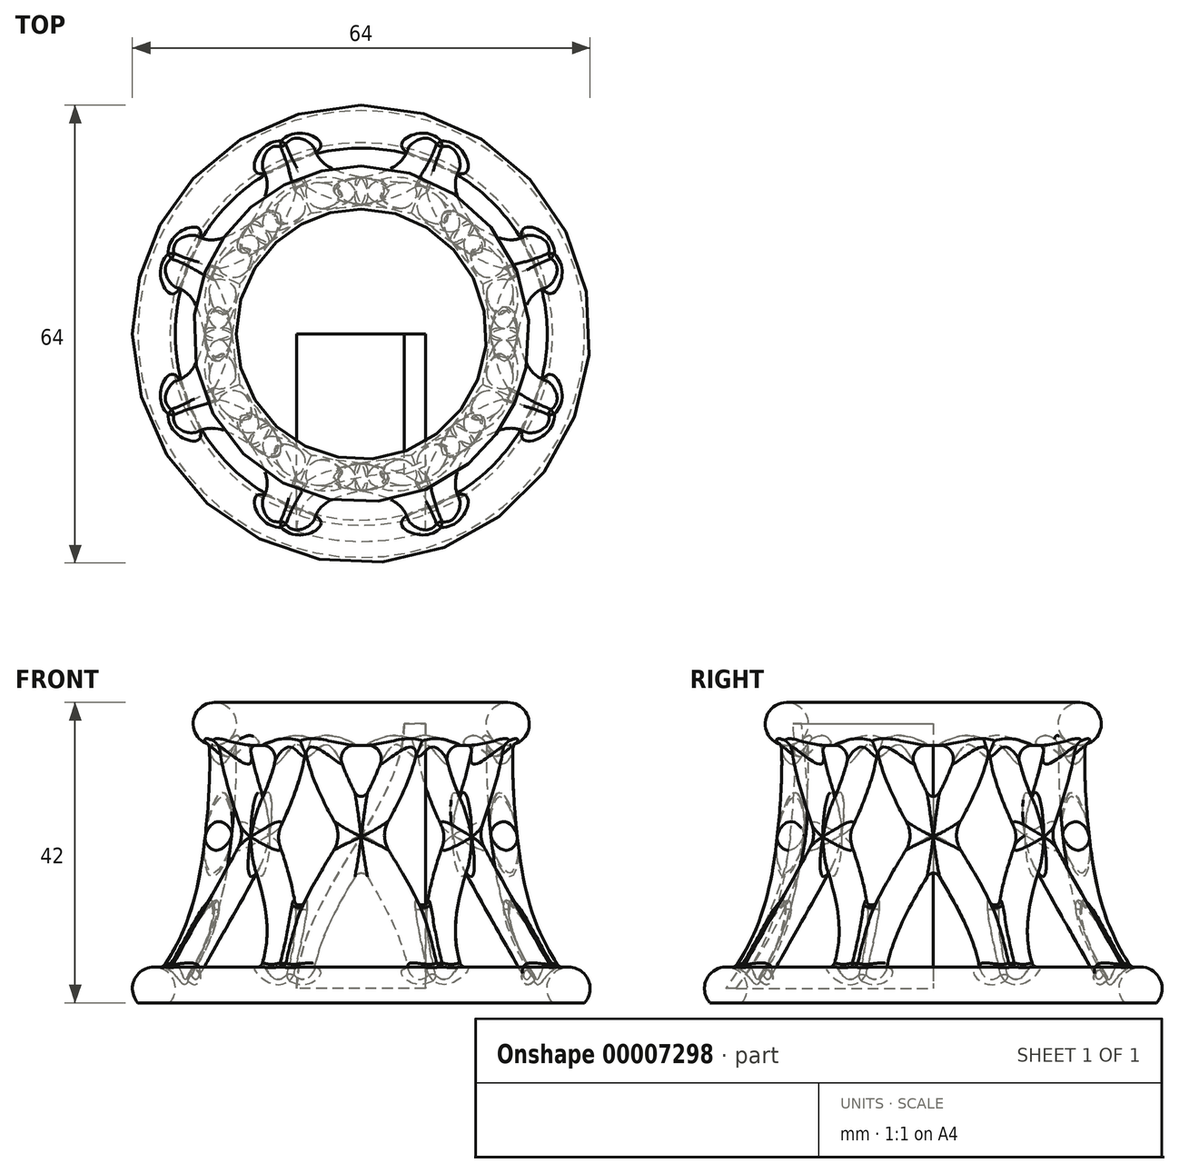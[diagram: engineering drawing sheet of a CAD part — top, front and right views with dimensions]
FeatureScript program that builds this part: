
annotation { "Feature Type Name" : "Feature", "Feature Type Description" : "" }
export const myFeature = defineFeature(function(context is Context, id is Id, definition is map)
    precondition{}
    {
        {
            var Q0;
            Q0=qCreatedBy(makeId("Front.planeOp"),FACE);
            var sketch = newSketch(context, id + "F0", { "sketchPlane" : qUnion([Q0])});
            skLineSegment(sketch, "E0", {"start": v(0, 0) * mm, "end": v(0, 10.66) * mm, "construction": true});
            skArc(sketch, "E1", {"start": v(31.24, 0) * mm, "mid": v(29, 5) * mm, "end": v(26.76, 0) * mm});
            skLineSegment(sketch, "E2", {"start": v(26.76, 0) * mm, "end": v(31.24, 0) * mm});
            skLineSegment(sketch, "E3", {"start": v(29, 2) * mm, "end": v(32, 2) * mm, "construction": true});
            skSolve(sketch);
        }
        {
            var Q0;
            Q0=makeQuery(id+"F0.imprint","IMPRINT",FACE,{"disambiguationData":[TD([[makeQuery(id+"F0.imprint","IMPRINT",EDGE,{"derivedFrom":sQuery(id+"F0.wireOp",EDGE,"E1")}),1.0]])]});
            var Q1;
            Q1=sQuery(id+"F0.wireOp",EDGE,"E0");
            revolve(context, id + "F1", {"entities" : qUnion([Q0]), "axis" : qUnion([Q1]), "revolveType" : RevolveType.FULL});
        }
        {
            var Q0;
            Q0=qCreatedBy(makeId("Front.planeOp"),FACE);
            var sketch = newSketch(context, id + "F2", { "sketchPlane" : qUnion([Q0])});
            skCircle(sketch, "E4", {"center": v(20.5, 39) * mm, "radius": 3 * mm});
            skLineSegment(sketch, "E5", {"start": v(20.5, 39) * mm, "end": v(17.5, 39) * mm, "construction": true});
            skLineSegment(sketch, "E6", {"start": v(20.5, 39) * mm, "end": v(20.5, 42) * mm, "construction": true});
            skSolve(sketch);
        }
        {
            var Q0;
            Q0=makeQuery(id+"F2.imprint","IMPRINT",FACE,{"disambiguationData":[TD([[makeQuery(id+"F2.imprint","IMPRINT",EDGE,{"derivedFrom":sQuery(id+"F2.wireOp",EDGE,"E4")}),1.0]])]});
            var Q1;
            Q1=sQuery(id+"F0.wireOp",EDGE,"E0");
            revolve(context, id + "F3", {"entities" : qUnion([Q0]), "axis" : qUnion([Q1]), "revolveType" : RevolveType.FULL});
        }
        {
            var Q0;
            Q0=qCreatedBy(makeId("Front.planeOp"),FACE);
            var sketch = newSketch(context, id + "F4", { "sketchPlane" : qUnion([Q0])});
            skFitSpline(sketch, "E7", {"points": [v(6, 39) * mm, v(-9, 2) * mm], "startDerivative": vector(0, -36) * mm, "endDerivative": vector(0, -39) * mm});
            skLineSegment(sketch, "E8", {"start": v(0, 0) * mm, "end": v(-9, 0) * mm, "construction": true});
            skLineSegment(sketch, "E9", {"start": v(-9, 0) * mm, "end": v(-9, 2) * mm, "construction": true});
            skLineSegment(sketch, "E10", {"start": v(-9, 2) * mm, "end": v(-9, 39) * mm, "construction": true});
            skLineSegment(sketch, "E11", {"start": v(-9, 39) * mm, "end": v(6, 39) * mm, "construction": true});
            skLineSegment(sketch, "E12", {"start": v(0, 0) * mm, "end": v(0, 39) * mm, "construction": true});
            skLineSegment(sketch, "E13", {"start": v(6, 39) * mm, "end": v(6, 46.33) * mm, "construction": true});
            skLineSegment(sketch, "E14", {"start": v(6, 39) * mm, "end": v(9, 39) * mm});
            skLineSegment(sketch, "E15", {"start": v(9, 39) * mm, "end": v(9, 2) * mm});
            skLineSegment(sketch, "E16", {"start": v(9, 2) * mm, "end": v(-9, 2) * mm});
            skSolve(sketch);
        }
        {
            var Q0;
            Q0=qCreatedBy(makeId("Front.planeOp"),FACE);
            var sketch = newSketch(context, id + "F5", { "sketchPlane" : qUnion([Q0])});
            skFitSpline(sketch, "E17", {"points": [v(20.5, 39) * mm, v(29, 2) * mm], "startDerivative": vector(-3.15, -36) * mm, "endDerivative": vector(33.6, -48) * mm});
            skLineSegment(sketch, "E18", {"start": v(20.5, 39) * mm, "end": v(21.48, 50.2) * mm, "construction": true});
            skLineSegment(sketch, "E19", {"start": v(29, 2) * mm, "end": v(34.24, -5.49) * mm, "construction": true});
            skLineSegment(sketch, "E20", {"start": v(29, 2) * mm, "end": v(42.16, 2) * mm, "construction": true});
            skLineSegment(sketch, "E21", {"start": v(20.5, 39) * mm, "end": v(10.06, 39) * mm, "construction": true});
            skSolve(sketch);
        }
        {
            var Q0;
            Q0=sQuery(id+"F5.wireOp",EDGE,"E17");
            var Q1;
            Q1=sQuery(id+"F0.wireOp",EDGE,"E0");
            revolve(context, id + "F6", {"bodyType" : ToolBodyType.SURFACE, "surfaceEntities" : qUnion([Q0]), "axis" : qUnion([Q1]), "revolveType" : RevolveType.ONE_DIRECTION, "oppositeDirection" : true, "angle" : 180 * degree});
        }
        {
            var Q0;
            Q0=makeQuery(id+"F4.imprint","IMPRINT",FACE,{"disambiguationData":[TD([[makeQuery(id+"F4.imprint","IMPRINT",EDGE,{"derivedFrom":sQuery(id+"F4.wireOp",EDGE,"E7")}),1.0]])]});
            var Q1;
            Q1=makeQuery(id+"F6.opRevolve","SWEPT_FACE",FACE,{"disambiguationData":[OSD([sQuery(id+"F5.wireOp",EDGE,"E17")])]});
            extrude(context, id + "F7", {"entities" : qUnion([Q0]), "endBound" : BoundingType.UP_TO_SURFACE, "endBoundEntityFace" : qUnion([Q1]), "depth" : 25 * mm});
        }
        {
            var Q0;
            Q0=makeQuery(id+"F7.opExtrude","SWEPT_FACE",FACE,{"disambiguationData":[OSD([sQuery(id+"F4.wireOp",EDGE,"E16")])]});
            var sketch = newSketch(context, id + "F8", { "sketchPlane" : qUnion([Q0])});
            skCircle(sketch, "E22", {"center": v(-9, 27.57) * mm, "radius": 2.25 * mm});
            skSolve(sketch);
        }
        {
            var Q0;
            {var subQ0=sQuery(id+"F4.wireOp",EDGE,"E16");var subQ1=makeQuery(id+"F7.opExtrude","CAP_EDGE",EDGE,{"disambiguationData":[OSD([subQ0])],"isStart":false});var subQ2=sQuery(id+"F8.wireOp",EDGE,"E22");var subQ3=makeQuery(id+"F8.imprint","INTERSECT",VERTEX,{"derivedFrom":[subQ1,subQ2]});Q0=makeQuery(id+"F8.imprint","IMPRINT",FACE,{"disambiguationData":[TD([[makeQuery(id+"F8.imprint","IMPRINT",EDGE,{"disambiguationData":[TD([[subQ3,-1.0]])],"derivedFrom":subQ2}),1.0]])]});}
            var Q1;
            {var subQ0=sQuery(id+"F4.wireOp",EDGE,"E16");var subQ1=makeQuery(id+"F7.opExtrude","CAP_EDGE",EDGE,{"disambiguationData":[OSD([subQ0])],"isStart":false});var subQ2=sQuery(id+"F8.wireOp",EDGE,"E22");var subQ3=makeQuery(id+"F8.imprint","INTERSECT",VERTEX,{"derivedFrom":[subQ1,subQ2]});Q1=makeQuery(id+"F8.imprint","IMPRINT",FACE,{"disambiguationData":[TD([[makeQuery(id+"F8.imprint","IMPRINT",EDGE,{"disambiguationData":[TD([[subQ3,1.0]])],"derivedFrom":subQ2}),1.0]])]});}
            var Q2;
            Q2=makeQuery(id+"F7.opExtrude","CAP_EDGE",EDGE,{"disambiguationData":[OSD([sQuery(id+"F4.wireOp",EDGE,"E7")])],"isStart":false});
            sweep(context, id + "F9", {"profiles" : qUnion([Q0, Q1]), "path" : qUnion([Q2])});
        }
        {
            var Q0;
            Q0=makeQuery(id+"F9.opSweep","SWEPT_BODY",BODY,{"disambiguationData":[OSD([sQuery(id+"F4.wireOp",EDGE,"E7"),sQuery(id+"F8.wireOp",EDGE,"E22")])]});
            var Q1;
            Q1=qCreatedBy(makeId("Right.planeOp"),FACE);
            mirror(context, id + "F10", {"entities" : qUnion([Q0]), "mirrorPlane" : qUnion([Q1])});
        }
        {
            var Q0;
            Q0=makeQuery(id+"F9.opSweep","SWEPT_BODY",BODY,{"disambiguationData":[OSD([sQuery(id+"F4.wireOp",EDGE,"E7"),sQuery(id+"F8.wireOp",EDGE,"E22")])]});
            var Q1;
            Q1=makeQuery(id+"F10.opPattern","COPY",BODY,{"derivedFrom":makeQuery(id+"F9.opSweep","SWEPT_BODY",BODY,{"disambiguationData":[OSD([sQuery(id+"F4.wireOp",EDGE,"E7"),sQuery(id+"F8.wireOp",EDGE,"E22")])]}),"instanceName":"1"});
            booleanBodies(context, id + "F11", {"operationType" : BooleanOperationType.UNION, "tools" : qUnion([Q0, Q1])});
        }
        {
            var Q0;
            {var subQ0=makeQuery(id+"F9.opSweep","SWEPT_FACE",FACE,{"disambiguationData":[OSD([sQuery(id+"F4.wireOp",EDGE,"E7"),sQuery(id+"F8.wireOp",EDGE,"E22")])]});Q0=makeQuery(id+"F11.opBoolean","INTERSECT",EDGE,{"disambiguationData":[OD(0.0)],"derivedFrom":[subQ0,makeQuery(id+"F10.opPattern","COPY",FACE,{"derivedFrom":subQ0,"instanceName":"1"})]});}
            var Q1;
            {var subQ0=makeQuery(id+"F9.opSweep","SWEPT_FACE",FACE,{"disambiguationData":[OSD([sQuery(id+"F4.wireOp",EDGE,"E7"),sQuery(id+"F8.wireOp",EDGE,"E22")])]});Q1=makeQuery(id+"F11.opBoolean","INTERSECT",EDGE,{"disambiguationData":[OD(3.0)],"derivedFrom":[subQ0,makeQuery(id+"F10.opPattern","COPY",FACE,{"derivedFrom":subQ0,"instanceName":"1"})]});}
            fillet(context, id + "F12", {"entities" : qUnion([Q0, Q1]), "radius" : 1 * mm, "tangentPropagation" : true, "allowEdgeOverflow" : false});
        }
        {
            var Q0;
            {var subQ0=makeQuery(id+"F9.opSweep","SWEPT_FACE",FACE,{"disambiguationData":[OSD([sQuery(id+"F4.wireOp",EDGE,"E7"),sQuery(id+"F8.wireOp",EDGE,"E22")])]});Q0=makeQuery(id+"F11.opBoolean","INTERSECT",EDGE,{"disambiguationData":[OD(2.0)],"derivedFrom":[subQ0,makeQuery(id+"F10.opPattern","COPY",FACE,{"derivedFrom":subQ0,"instanceName":"1"})]});}
            var Q1;
            {var subQ0=makeQuery(id+"F9.opSweep","SWEPT_FACE",FACE,{"disambiguationData":[OSD([sQuery(id+"F4.wireOp",EDGE,"E7"),sQuery(id+"F8.wireOp",EDGE,"E22")])]});Q1=makeQuery(id+"F11.opBoolean","INTERSECT",EDGE,{"disambiguationData":[OD(1.0)],"derivedFrom":[subQ0,makeQuery(id+"F10.opPattern","COPY",FACE,{"derivedFrom":subQ0,"instanceName":"1"})]});}
            fillet(context, id + "F13", {"entities" : qUnion([Q0, Q1]), "radius" : 4 * mm, "tangentPropagation" : true, "allowEdgeOverflow" : false});
        }
        {
            var Q0;
            Q0=makeQuery(id+"F9.opSweep","SWEPT_BODY",BODY,{"disambiguationData":[OSD([sQuery(id+"F4.wireOp",EDGE,"E7"),sQuery(id+"F8.wireOp",EDGE,"E22")])]});
            var Q1;
            Q1=sQuery(id+"F0.wireOp",EDGE,"E0");
            circularPattern(context, id + "F14", {"entities" : qUnion([Q0]), "axis" : qUnion([Q1]), "angle" : 45 * degree, "instanceCount" : 8});
        }
        {
            var Q0;
            Q0=makeQuery(id+"F14.opPattern","COPY",BODY,{"derivedFrom":makeQuery(id+"F9.opSweep","SWEPT_BODY",BODY,{"disambiguationData":[OSD([sQuery(id+"F4.wireOp",EDGE,"E7"),sQuery(id+"F8.wireOp",EDGE,"E22")])]}),"instanceName":"1"});
            var Q1;
            Q1=makeQuery(id+"F14.opPattern","COPY",BODY,{"derivedFrom":makeQuery(id+"F9.opSweep","SWEPT_BODY",BODY,{"disambiguationData":[OSD([sQuery(id+"F4.wireOp",EDGE,"E7"),sQuery(id+"F8.wireOp",EDGE,"E22")])]}),"instanceName":"2"});
            var Q2;
            Q2=makeQuery(id+"F9.opSweep","SWEPT_BODY",BODY,{"disambiguationData":[OSD([sQuery(id+"F4.wireOp",EDGE,"E7"),sQuery(id+"F8.wireOp",EDGE,"E22")])]});
            var Q3;
            Q3=makeQuery(id+"F14.opPattern","COPY",BODY,{"derivedFrom":makeQuery(id+"F9.opSweep","SWEPT_BODY",BODY,{"disambiguationData":[OSD([sQuery(id+"F4.wireOp",EDGE,"E7"),sQuery(id+"F8.wireOp",EDGE,"E22")])]}),"instanceName":"7"});
            var Q4;
            Q4=makeQuery(id+"F1.opRevolve","SWEPT_BODY",BODY,{"disambiguationData":[OSD([sQuery(id+"F0.wireOp",EDGE,"E1"),sQuery(id+"F0.wireOp",EDGE,"E2")])]});
            var Q5;
            Q5=makeQuery(id+"F3.opRevolve","SWEPT_BODY",BODY,{"disambiguationData":[OSD([sQuery(id+"F2.wireOp",EDGE,"E4")])]});
            var Q6;
            Q6=makeQuery(id+"F14.opPattern","COPY",BODY,{"derivedFrom":makeQuery(id+"F9.opSweep","SWEPT_BODY",BODY,{"disambiguationData":[OSD([sQuery(id+"F4.wireOp",EDGE,"E7"),sQuery(id+"F8.wireOp",EDGE,"E22")])]}),"instanceName":"3"});
            var Q7;
            Q7=makeQuery(id+"F14.opPattern","COPY",BODY,{"derivedFrom":makeQuery(id+"F9.opSweep","SWEPT_BODY",BODY,{"disambiguationData":[OSD([sQuery(id+"F4.wireOp",EDGE,"E7"),sQuery(id+"F8.wireOp",EDGE,"E22")])]}),"instanceName":"4"});
            var Q8;
            Q8=makeQuery(id+"F14.opPattern","COPY",BODY,{"derivedFrom":makeQuery(id+"F9.opSweep","SWEPT_BODY",BODY,{"disambiguationData":[OSD([sQuery(id+"F4.wireOp",EDGE,"E7"),sQuery(id+"F8.wireOp",EDGE,"E22")])]}),"instanceName":"5"});
            var Q9;
            Q9=makeQuery(id+"F14.opPattern","COPY",BODY,{"derivedFrom":makeQuery(id+"F9.opSweep","SWEPT_BODY",BODY,{"disambiguationData":[OSD([sQuery(id+"F4.wireOp",EDGE,"E7"),sQuery(id+"F8.wireOp",EDGE,"E22")])]}),"instanceName":"6"});
            booleanBodies(context, id + "F15", {"operationType" : BooleanOperationType.UNION, "tools" : qUnion([Q0, Q1, Q2, Q3, Q4, Q5, Q6, Q7, Q8, Q9])});
        }
        {
            var Q0;
            {var subQ0=sQuery(id+"F4.wireOp",EDGE,"E7");var subQ1=sQuery(id+"F8.wireOp",EDGE,"E22");var subQ2=makeQuery(id+"F9.opSweep","SWEPT_FACE",FACE,{"disambiguationData":[OSD([subQ0,subQ1])]});var subQ3=makeQuery(id+"F10.opPattern","COPY",FACE,{"derivedFrom":subQ2,"instanceName":"1"});Q0=makeQuery(id+"F15.opBoolean","INTERSECT",EDGE,{"disambiguationData":[OD(0.0)],"derivedFrom":[makeQuery(id+"F3.opRevolve","SWEPT_FACE",FACE,{"disambiguationData":[OSD([sQuery(id+"F2.wireOp",EDGE,"E4")])]}),makeQuery(id+"F14.opPattern","COPY",FACE,{"derivedFrom":makeQuery(id+"F11.opBoolean","SPLIT",FACE,{"disambiguationData":[TD([makeQuery(id+"F10.opPattern","COPY",FACE,{"derivedFrom":makeQuery(id+"F9.opSweep","CAP_FACE",FACE,{"disambiguationData":[OSD([subQ0,sQuery(id+"F4.wireOp",EDGE,"E14"),subQ1])],"isStart":false}),"instanceName":"1"})])],"derivedFrom":subQ3}),"instanceName":"6"})]});}
            var Q1;
            {var subQ0=sQuery(id+"F4.wireOp",EDGE,"E7");var subQ1=sQuery(id+"F8.wireOp",EDGE,"E22");var subQ2=makeQuery(id+"F9.opSweep","SWEPT_FACE",FACE,{"disambiguationData":[OSD([subQ0,subQ1])]});Q1=makeQuery(id+"F15.opBoolean","INTERSECT",EDGE,{"disambiguationData":[OD(0.0)],"derivedFrom":[makeQuery(id+"F3.opRevolve","SWEPT_FACE",FACE,{"disambiguationData":[OSD([sQuery(id+"F2.wireOp",EDGE,"E4")])]}),makeQuery(id+"F14.opPattern","COPY",FACE,{"derivedFrom":makeQuery(id+"F11.opBoolean","SPLIT",FACE,{"disambiguationData":[TD([makeQuery(id+"F9.opSweep","CAP_FACE",FACE,{"disambiguationData":[OSD([subQ0,sQuery(id+"F4.wireOp",EDGE,"E14"),subQ1])],"isStart":false})])],"derivedFrom":subQ2}),"instanceName":"6"})]});}
            var Q2;
            {var subQ0=sQuery(id+"F4.wireOp",EDGE,"E7");var subQ1=sQuery(id+"F8.wireOp",EDGE,"E22");var subQ2=makeQuery(id+"F9.opSweep","SWEPT_FACE",FACE,{"disambiguationData":[OSD([subQ0,subQ1])]});var subQ3=makeQuery(id+"F10.opPattern","COPY",FACE,{"derivedFrom":subQ2,"instanceName":"1"});Q2=makeQuery(id+"F15.opBoolean","INTERSECT",EDGE,{"disambiguationData":[OD(0.0)],"derivedFrom":[makeQuery(id+"F3.opRevolve","SWEPT_FACE",FACE,{"disambiguationData":[OSD([sQuery(id+"F2.wireOp",EDGE,"E4")])]}),makeQuery(id+"F14.opPattern","COPY",FACE,{"derivedFrom":makeQuery(id+"F11.opBoolean","SPLIT",FACE,{"disambiguationData":[TD([makeQuery(id+"F10.opPattern","COPY",FACE,{"derivedFrom":makeQuery(id+"F9.opSweep","CAP_FACE",FACE,{"disambiguationData":[OSD([subQ0,sQuery(id+"F4.wireOp",EDGE,"E14"),subQ1])],"isStart":false}),"instanceName":"1"})])],"derivedFrom":subQ3}),"instanceName":"7"})]});}
            var Q3;
            {var subQ0=sQuery(id+"F4.wireOp",EDGE,"E7");var subQ1=sQuery(id+"F8.wireOp",EDGE,"E22");var subQ2=makeQuery(id+"F9.opSweep","SWEPT_FACE",FACE,{"disambiguationData":[OSD([subQ0,subQ1])]});Q3=makeQuery(id+"F15.opBoolean","INTERSECT",EDGE,{"disambiguationData":[OD(0.0)],"derivedFrom":[makeQuery(id+"F3.opRevolve","SWEPT_FACE",FACE,{"disambiguationData":[OSD([sQuery(id+"F2.wireOp",EDGE,"E4")])]}),makeQuery(id+"F14.opPattern","COPY",FACE,{"derivedFrom":makeQuery(id+"F11.opBoolean","SPLIT",FACE,{"disambiguationData":[TD([makeQuery(id+"F9.opSweep","CAP_FACE",FACE,{"disambiguationData":[OSD([subQ0,sQuery(id+"F4.wireOp",EDGE,"E14"),subQ1])],"isStart":false})])],"derivedFrom":subQ2}),"instanceName":"7"})]});}
            var Q4;
            {var subQ0=sQuery(id+"F4.wireOp",EDGE,"E7");var subQ1=sQuery(id+"F8.wireOp",EDGE,"E22");var subQ2=makeQuery(id+"F9.opSweep","SWEPT_FACE",FACE,{"disambiguationData":[OSD([subQ0,subQ1])]});var subQ3=makeQuery(id+"F10.opPattern","COPY",FACE,{"derivedFrom":subQ2,"instanceName":"1"});Q4=makeQuery(id+"F15.opBoolean","INTERSECT",EDGE,{"disambiguationData":[OD(0.0)],"derivedFrom":[makeQuery(id+"F3.opRevolve","SWEPT_FACE",FACE,{"disambiguationData":[OSD([sQuery(id+"F2.wireOp",EDGE,"E4")])]}),makeQuery(id+"F11.opBoolean","SPLIT",FACE,{"disambiguationData":[TD([makeQuery(id+"F10.opPattern","COPY",FACE,{"derivedFrom":makeQuery(id+"F9.opSweep","CAP_FACE",FACE,{"disambiguationData":[OSD([subQ0,sQuery(id+"F4.wireOp",EDGE,"E14"),subQ1])],"isStart":false}),"instanceName":"1"})])],"derivedFrom":subQ3})]});}
            var Q5;
            {var subQ0=sQuery(id+"F4.wireOp",EDGE,"E7");var subQ1=sQuery(id+"F8.wireOp",EDGE,"E22");var subQ2=makeQuery(id+"F9.opSweep","SWEPT_FACE",FACE,{"disambiguationData":[OSD([subQ0,subQ1])]});Q5=makeQuery(id+"F15.opBoolean","INTERSECT",EDGE,{"disambiguationData":[OD(0.0)],"derivedFrom":[makeQuery(id+"F3.opRevolve","SWEPT_FACE",FACE,{"disambiguationData":[OSD([sQuery(id+"F2.wireOp",EDGE,"E4")])]}),makeQuery(id+"F11.opBoolean","SPLIT",FACE,{"disambiguationData":[TD([makeQuery(id+"F9.opSweep","CAP_FACE",FACE,{"disambiguationData":[OSD([subQ0,sQuery(id+"F4.wireOp",EDGE,"E14"),subQ1])],"isStart":false})])],"derivedFrom":subQ2})]});}
            var Q6;
            {var subQ0=sQuery(id+"F4.wireOp",EDGE,"E7");var subQ1=sQuery(id+"F8.wireOp",EDGE,"E22");var subQ2=makeQuery(id+"F9.opSweep","SWEPT_FACE",FACE,{"disambiguationData":[OSD([subQ0,subQ1])]});Q6=makeQuery(id+"F15.opBoolean","INTERSECT",EDGE,{"disambiguationData":[OD(0.0)],"derivedFrom":[makeQuery(id+"F3.opRevolve","SWEPT_FACE",FACE,{"disambiguationData":[OSD([sQuery(id+"F2.wireOp",EDGE,"E4")])]}),makeQuery(id+"F14.opPattern","COPY",FACE,{"derivedFrom":makeQuery(id+"F11.opBoolean","SPLIT",FACE,{"disambiguationData":[TD([makeQuery(id+"F9.opSweep","CAP_FACE",FACE,{"disambiguationData":[OSD([subQ0,sQuery(id+"F4.wireOp",EDGE,"E14"),subQ1])],"isStart":false})])],"derivedFrom":subQ2}),"instanceName":"1"})]});}
            var Q7;
            {var subQ0=sQuery(id+"F4.wireOp",EDGE,"E7");var subQ1=sQuery(id+"F8.wireOp",EDGE,"E22");var subQ2=makeQuery(id+"F9.opSweep","SWEPT_FACE",FACE,{"disambiguationData":[OSD([subQ0,subQ1])]});var subQ3=makeQuery(id+"F10.opPattern","COPY",FACE,{"derivedFrom":subQ2,"instanceName":"1"});Q7=makeQuery(id+"F15.opBoolean","INTERSECT",EDGE,{"disambiguationData":[OD(0.0)],"derivedFrom":[makeQuery(id+"F3.opRevolve","SWEPT_FACE",FACE,{"disambiguationData":[OSD([sQuery(id+"F2.wireOp",EDGE,"E4")])]}),makeQuery(id+"F14.opPattern","COPY",FACE,{"derivedFrom":makeQuery(id+"F11.opBoolean","SPLIT",FACE,{"disambiguationData":[TD([makeQuery(id+"F10.opPattern","COPY",FACE,{"derivedFrom":makeQuery(id+"F9.opSweep","CAP_FACE",FACE,{"disambiguationData":[OSD([subQ0,sQuery(id+"F4.wireOp",EDGE,"E14"),subQ1])],"isStart":false}),"instanceName":"1"})])],"derivedFrom":subQ3}),"instanceName":"1"})]});}
            var Q8;
            {var subQ0=sQuery(id+"F4.wireOp",EDGE,"E7");var subQ1=sQuery(id+"F8.wireOp",EDGE,"E22");var subQ2=makeQuery(id+"F9.opSweep","SWEPT_FACE",FACE,{"disambiguationData":[OSD([subQ0,subQ1])]});Q8=makeQuery(id+"F15.opBoolean","INTERSECT",EDGE,{"disambiguationData":[OD(0.0)],"derivedFrom":[makeQuery(id+"F3.opRevolve","SWEPT_FACE",FACE,{"disambiguationData":[OSD([sQuery(id+"F2.wireOp",EDGE,"E4")])]}),makeQuery(id+"F14.opPattern","COPY",FACE,{"derivedFrom":makeQuery(id+"F11.opBoolean","SPLIT",FACE,{"disambiguationData":[TD([makeQuery(id+"F9.opSweep","CAP_FACE",FACE,{"disambiguationData":[OSD([subQ0,sQuery(id+"F4.wireOp",EDGE,"E14"),subQ1])],"isStart":false})])],"derivedFrom":subQ2}),"instanceName":"2"})]});}
            var Q9;
            {var subQ0=sQuery(id+"F4.wireOp",EDGE,"E7");var subQ1=sQuery(id+"F8.wireOp",EDGE,"E22");var subQ2=makeQuery(id+"F9.opSweep","SWEPT_FACE",FACE,{"disambiguationData":[OSD([subQ0,subQ1])]});var subQ3=makeQuery(id+"F10.opPattern","COPY",FACE,{"derivedFrom":subQ2,"instanceName":"1"});Q9=makeQuery(id+"F15.opBoolean","INTERSECT",EDGE,{"disambiguationData":[OD(0.0)],"derivedFrom":[makeQuery(id+"F3.opRevolve","SWEPT_FACE",FACE,{"disambiguationData":[OSD([sQuery(id+"F2.wireOp",EDGE,"E4")])]}),makeQuery(id+"F14.opPattern","COPY",FACE,{"derivedFrom":makeQuery(id+"F11.opBoolean","SPLIT",FACE,{"disambiguationData":[TD([makeQuery(id+"F10.opPattern","COPY",FACE,{"derivedFrom":makeQuery(id+"F9.opSweep","CAP_FACE",FACE,{"disambiguationData":[OSD([subQ0,sQuery(id+"F4.wireOp",EDGE,"E14"),subQ1])],"isStart":false}),"instanceName":"1"})])],"derivedFrom":subQ3}),"instanceName":"2"})]});}
            var Q10;
            {var subQ0=sQuery(id+"F4.wireOp",EDGE,"E7");var subQ1=sQuery(id+"F8.wireOp",EDGE,"E22");var subQ2=makeQuery(id+"F9.opSweep","SWEPT_FACE",FACE,{"disambiguationData":[OSD([subQ0,subQ1])]});var subQ3=makeQuery(id+"F10.opPattern","COPY",FACE,{"derivedFrom":subQ2,"instanceName":"1"});Q10=makeQuery(id+"F15.opBoolean","INTERSECT",EDGE,{"disambiguationData":[OD(0.0)],"derivedFrom":[makeQuery(id+"F3.opRevolve","SWEPT_FACE",FACE,{"disambiguationData":[OSD([sQuery(id+"F2.wireOp",EDGE,"E4")])]}),makeQuery(id+"F14.opPattern","COPY",FACE,{"derivedFrom":makeQuery(id+"F11.opBoolean","SPLIT",FACE,{"disambiguationData":[TD([makeQuery(id+"F10.opPattern","COPY",FACE,{"derivedFrom":makeQuery(id+"F9.opSweep","CAP_FACE",FACE,{"disambiguationData":[OSD([subQ0,sQuery(id+"F4.wireOp",EDGE,"E14"),subQ1])],"isStart":false}),"instanceName":"1"})])],"derivedFrom":subQ3}),"instanceName":"3"})]});}
            var Q11;
            {var subQ0=sQuery(id+"F4.wireOp",EDGE,"E7");var subQ1=sQuery(id+"F8.wireOp",EDGE,"E22");var subQ2=makeQuery(id+"F9.opSweep","SWEPT_FACE",FACE,{"disambiguationData":[OSD([subQ0,subQ1])]});Q11=makeQuery(id+"F15.opBoolean","INTERSECT",EDGE,{"disambiguationData":[OD(0.0)],"derivedFrom":[makeQuery(id+"F3.opRevolve","SWEPT_FACE",FACE,{"disambiguationData":[OSD([sQuery(id+"F2.wireOp",EDGE,"E4")])]}),makeQuery(id+"F14.opPattern","COPY",FACE,{"derivedFrom":makeQuery(id+"F11.opBoolean","SPLIT",FACE,{"disambiguationData":[TD([makeQuery(id+"F9.opSweep","CAP_FACE",FACE,{"disambiguationData":[OSD([subQ0,sQuery(id+"F4.wireOp",EDGE,"E14"),subQ1])],"isStart":false})])],"derivedFrom":subQ2}),"instanceName":"3"})]});}
            var Q12;
            {var subQ0=sQuery(id+"F4.wireOp",EDGE,"E7");var subQ1=sQuery(id+"F8.wireOp",EDGE,"E22");var subQ2=makeQuery(id+"F9.opSweep","SWEPT_FACE",FACE,{"disambiguationData":[OSD([subQ0,subQ1])]});var subQ3=makeQuery(id+"F10.opPattern","COPY",FACE,{"derivedFrom":subQ2,"instanceName":"1"});Q12=makeQuery(id+"F15.opBoolean","INTERSECT",EDGE,{"disambiguationData":[OD(0.0)],"derivedFrom":[makeQuery(id+"F3.opRevolve","SWEPT_FACE",FACE,{"disambiguationData":[OSD([sQuery(id+"F2.wireOp",EDGE,"E4")])]}),makeQuery(id+"F14.opPattern","COPY",FACE,{"derivedFrom":makeQuery(id+"F11.opBoolean","SPLIT",FACE,{"disambiguationData":[TD([makeQuery(id+"F10.opPattern","COPY",FACE,{"derivedFrom":makeQuery(id+"F9.opSweep","CAP_FACE",FACE,{"disambiguationData":[OSD([subQ0,sQuery(id+"F4.wireOp",EDGE,"E14"),subQ1])],"isStart":false}),"instanceName":"1"})])],"derivedFrom":subQ3}),"instanceName":"4"})]});}
            var Q13;
            {var subQ0=sQuery(id+"F4.wireOp",EDGE,"E7");var subQ1=sQuery(id+"F8.wireOp",EDGE,"E22");var subQ2=makeQuery(id+"F9.opSweep","SWEPT_FACE",FACE,{"disambiguationData":[OSD([subQ0,subQ1])]});Q13=makeQuery(id+"F15.opBoolean","INTERSECT",EDGE,{"disambiguationData":[OD(0.0)],"derivedFrom":[makeQuery(id+"F3.opRevolve","SWEPT_FACE",FACE,{"disambiguationData":[OSD([sQuery(id+"F2.wireOp",EDGE,"E4")])]}),makeQuery(id+"F14.opPattern","COPY",FACE,{"derivedFrom":makeQuery(id+"F11.opBoolean","SPLIT",FACE,{"disambiguationData":[TD([makeQuery(id+"F9.opSweep","CAP_FACE",FACE,{"disambiguationData":[OSD([subQ0,sQuery(id+"F4.wireOp",EDGE,"E14"),subQ1])],"isStart":false})])],"derivedFrom":subQ2}),"instanceName":"4"})]});}
            var Q14;
            {var subQ0=sQuery(id+"F4.wireOp",EDGE,"E7");var subQ1=sQuery(id+"F8.wireOp",EDGE,"E22");var subQ2=makeQuery(id+"F9.opSweep","SWEPT_FACE",FACE,{"disambiguationData":[OSD([subQ0,subQ1])]});var subQ3=makeQuery(id+"F10.opPattern","COPY",FACE,{"derivedFrom":subQ2,"instanceName":"1"});Q14=makeQuery(id+"F15.opBoolean","INTERSECT",EDGE,{"disambiguationData":[OD(0.0)],"derivedFrom":[makeQuery(id+"F3.opRevolve","SWEPT_FACE",FACE,{"disambiguationData":[OSD([sQuery(id+"F2.wireOp",EDGE,"E4")])]}),makeQuery(id+"F14.opPattern","COPY",FACE,{"derivedFrom":makeQuery(id+"F11.opBoolean","SPLIT",FACE,{"disambiguationData":[TD([makeQuery(id+"F10.opPattern","COPY",FACE,{"derivedFrom":makeQuery(id+"F9.opSweep","CAP_FACE",FACE,{"disambiguationData":[OSD([subQ0,sQuery(id+"F4.wireOp",EDGE,"E14"),subQ1])],"isStart":false}),"instanceName":"1"})])],"derivedFrom":subQ3}),"instanceName":"5"})]});}
            var Q15;
            {var subQ0=sQuery(id+"F4.wireOp",EDGE,"E7");var subQ1=sQuery(id+"F8.wireOp",EDGE,"E22");var subQ2=makeQuery(id+"F9.opSweep","SWEPT_FACE",FACE,{"disambiguationData":[OSD([subQ0,subQ1])]});Q15=makeQuery(id+"F15.opBoolean","INTERSECT",EDGE,{"disambiguationData":[OD(0.0)],"derivedFrom":[makeQuery(id+"F3.opRevolve","SWEPT_FACE",FACE,{"disambiguationData":[OSD([sQuery(id+"F2.wireOp",EDGE,"E4")])]}),makeQuery(id+"F14.opPattern","COPY",FACE,{"derivedFrom":makeQuery(id+"F11.opBoolean","SPLIT",FACE,{"disambiguationData":[TD([makeQuery(id+"F9.opSweep","CAP_FACE",FACE,{"disambiguationData":[OSD([subQ0,sQuery(id+"F4.wireOp",EDGE,"E14"),subQ1])],"isStart":false})])],"derivedFrom":subQ2}),"instanceName":"5"})]});}
            fillet(context, id + "F16", {"entities" : qUnion([Q0, Q1, Q2, Q3, Q4, Q5, Q6, Q7, Q8, Q9, Q10, Q11, Q12, Q13, Q14, Q15]), "radius" : 2 * mm, "tangentPropagation" : true, "allowEdgeOverflow" : false});
        }
        {
            var Q0;
            {var subQ0=sQuery(id+"F4.wireOp",EDGE,"E7");var subQ1=sQuery(id+"F8.wireOp",EDGE,"E22");var subQ2=makeQuery(id+"F9.opSweep","SWEPT_FACE",FACE,{"disambiguationData":[OSD([subQ0,subQ1])]});Q0=makeQuery(id+"F15.opBoolean","INTERSECT",EDGE,{"disambiguationData":[OD(0.0)],"derivedFrom":[makeQuery(id+"F1.opRevolve","SWEPT_FACE",FACE,{"disambiguationData":[OSD([sQuery(id+"F0.wireOp",EDGE,"E1")])]}),makeQuery(id+"F14.opPattern","COPY",FACE,{"derivedFrom":makeQuery(id+"F11.opBoolean","SPLIT",FACE,{"disambiguationData":[TD([makeQuery(id+"F9.opSweep","CAP_FACE",FACE,{"disambiguationData":[OSD([subQ0,sQuery(id+"F4.wireOp",EDGE,"E16"),subQ1])],"isStart":true})])],"derivedFrom":subQ2}),"instanceName":"5"})]});}
            var Q1;
            {var subQ0=sQuery(id+"F4.wireOp",EDGE,"E7");var subQ1=sQuery(id+"F8.wireOp",EDGE,"E22");var subQ2=makeQuery(id+"F9.opSweep","SWEPT_FACE",FACE,{"disambiguationData":[OSD([subQ0,subQ1])]});var subQ3=makeQuery(id+"F10.opPattern","COPY",FACE,{"derivedFrom":subQ2,"instanceName":"1"});Q1=makeQuery(id+"F15.opBoolean","INTERSECT",EDGE,{"disambiguationData":[OD(0.0)],"derivedFrom":[makeQuery(id+"F1.opRevolve","SWEPT_FACE",FACE,{"disambiguationData":[OSD([sQuery(id+"F0.wireOp",EDGE,"E1")])]}),makeQuery(id+"F14.opPattern","COPY",FACE,{"derivedFrom":makeQuery(id+"F11.opBoolean","SPLIT",FACE,{"disambiguationData":[TD([makeQuery(id+"F10.opPattern","COPY",FACE,{"derivedFrom":makeQuery(id+"F9.opSweep","CAP_FACE",FACE,{"disambiguationData":[OSD([subQ0,sQuery(id+"F4.wireOp",EDGE,"E16"),subQ1])],"isStart":true}),"instanceName":"1"})])],"derivedFrom":subQ3}),"instanceName":"5"})]});}
            var Q2;
            {var subQ0=sQuery(id+"F4.wireOp",EDGE,"E7");var subQ1=sQuery(id+"F8.wireOp",EDGE,"E22");var subQ2=makeQuery(id+"F9.opSweep","SWEPT_FACE",FACE,{"disambiguationData":[OSD([subQ0,subQ1])]});Q2=makeQuery(id+"F15.opBoolean","INTERSECT",EDGE,{"disambiguationData":[OD(0.0)],"derivedFrom":[makeQuery(id+"F1.opRevolve","SWEPT_FACE",FACE,{"disambiguationData":[OSD([sQuery(id+"F0.wireOp",EDGE,"E1")])]}),makeQuery(id+"F14.opPattern","COPY",FACE,{"derivedFrom":makeQuery(id+"F11.opBoolean","SPLIT",FACE,{"disambiguationData":[TD([makeQuery(id+"F9.opSweep","CAP_FACE",FACE,{"disambiguationData":[OSD([subQ0,sQuery(id+"F4.wireOp",EDGE,"E16"),subQ1])],"isStart":true})])],"derivedFrom":subQ2}),"instanceName":"6"})]});}
            var Q3;
            {var subQ0=sQuery(id+"F4.wireOp",EDGE,"E7");var subQ1=sQuery(id+"F8.wireOp",EDGE,"E22");var subQ2=makeQuery(id+"F9.opSweep","SWEPT_FACE",FACE,{"disambiguationData":[OSD([subQ0,subQ1])]});var subQ3=makeQuery(id+"F10.opPattern","COPY",FACE,{"derivedFrom":subQ2,"instanceName":"1"});Q3=makeQuery(id+"F15.opBoolean","INTERSECT",EDGE,{"disambiguationData":[OD(0.0)],"derivedFrom":[makeQuery(id+"F1.opRevolve","SWEPT_FACE",FACE,{"disambiguationData":[OSD([sQuery(id+"F0.wireOp",EDGE,"E1")])]}),makeQuery(id+"F14.opPattern","COPY",FACE,{"derivedFrom":makeQuery(id+"F11.opBoolean","SPLIT",FACE,{"disambiguationData":[TD([makeQuery(id+"F10.opPattern","COPY",FACE,{"derivedFrom":makeQuery(id+"F9.opSweep","CAP_FACE",FACE,{"disambiguationData":[OSD([subQ0,sQuery(id+"F4.wireOp",EDGE,"E16"),subQ1])],"isStart":true}),"instanceName":"1"})])],"derivedFrom":subQ3}),"instanceName":"6"})]});}
            var Q4;
            {var subQ0=sQuery(id+"F4.wireOp",EDGE,"E7");var subQ1=sQuery(id+"F8.wireOp",EDGE,"E22");var subQ2=makeQuery(id+"F9.opSweep","SWEPT_FACE",FACE,{"disambiguationData":[OSD([subQ0,subQ1])]});Q4=makeQuery(id+"F15.opBoolean","INTERSECT",EDGE,{"disambiguationData":[OD(0.0)],"derivedFrom":[makeQuery(id+"F1.opRevolve","SWEPT_FACE",FACE,{"disambiguationData":[OSD([sQuery(id+"F0.wireOp",EDGE,"E1")])]}),makeQuery(id+"F14.opPattern","COPY",FACE,{"derivedFrom":makeQuery(id+"F11.opBoolean","SPLIT",FACE,{"disambiguationData":[TD([makeQuery(id+"F9.opSweep","CAP_FACE",FACE,{"disambiguationData":[OSD([subQ0,sQuery(id+"F4.wireOp",EDGE,"E16"),subQ1])],"isStart":true})])],"derivedFrom":subQ2}),"instanceName":"7"})]});}
            var Q5;
            {var subQ0=sQuery(id+"F4.wireOp",EDGE,"E7");var subQ1=sQuery(id+"F8.wireOp",EDGE,"E22");var subQ2=makeQuery(id+"F9.opSweep","SWEPT_FACE",FACE,{"disambiguationData":[OSD([subQ0,subQ1])]});var subQ3=makeQuery(id+"F10.opPattern","COPY",FACE,{"derivedFrom":subQ2,"instanceName":"1"});Q5=makeQuery(id+"F15.opBoolean","INTERSECT",EDGE,{"disambiguationData":[OD(0.0)],"derivedFrom":[makeQuery(id+"F1.opRevolve","SWEPT_FACE",FACE,{"disambiguationData":[OSD([sQuery(id+"F0.wireOp",EDGE,"E1")])]}),makeQuery(id+"F14.opPattern","COPY",FACE,{"derivedFrom":makeQuery(id+"F11.opBoolean","SPLIT",FACE,{"disambiguationData":[TD([makeQuery(id+"F10.opPattern","COPY",FACE,{"derivedFrom":makeQuery(id+"F9.opSweep","CAP_FACE",FACE,{"disambiguationData":[OSD([subQ0,sQuery(id+"F4.wireOp",EDGE,"E16"),subQ1])],"isStart":true}),"instanceName":"1"})])],"derivedFrom":subQ3}),"instanceName":"7"})]});}
            var Q6;
            {var subQ0=sQuery(id+"F4.wireOp",EDGE,"E7");var subQ1=sQuery(id+"F8.wireOp",EDGE,"E22");var subQ2=makeQuery(id+"F9.opSweep","SWEPT_FACE",FACE,{"disambiguationData":[OSD([subQ0,subQ1])]});Q6=makeQuery(id+"F15.opBoolean","INTERSECT",EDGE,{"disambiguationData":[OD(0.0)],"derivedFrom":[makeQuery(id+"F1.opRevolve","SWEPT_FACE",FACE,{"disambiguationData":[OSD([sQuery(id+"F0.wireOp",EDGE,"E1")])]}),makeQuery(id+"F11.opBoolean","SPLIT",FACE,{"disambiguationData":[TD([makeQuery(id+"F9.opSweep","CAP_FACE",FACE,{"disambiguationData":[OSD([subQ0,sQuery(id+"F4.wireOp",EDGE,"E16"),subQ1])],"isStart":true})])],"derivedFrom":subQ2})]});}
            var Q7;
            {var subQ0=sQuery(id+"F4.wireOp",EDGE,"E7");var subQ1=sQuery(id+"F8.wireOp",EDGE,"E22");var subQ2=makeQuery(id+"F9.opSweep","SWEPT_FACE",FACE,{"disambiguationData":[OSD([subQ0,subQ1])]});var subQ3=makeQuery(id+"F10.opPattern","COPY",FACE,{"derivedFrom":subQ2,"instanceName":"1"});Q7=makeQuery(id+"F15.opBoolean","INTERSECT",EDGE,{"disambiguationData":[OD(0.0)],"derivedFrom":[makeQuery(id+"F1.opRevolve","SWEPT_FACE",FACE,{"disambiguationData":[OSD([sQuery(id+"F0.wireOp",EDGE,"E1")])]}),makeQuery(id+"F11.opBoolean","SPLIT",FACE,{"disambiguationData":[TD([makeQuery(id+"F10.opPattern","COPY",FACE,{"derivedFrom":makeQuery(id+"F9.opSweep","CAP_FACE",FACE,{"disambiguationData":[OSD([subQ0,sQuery(id+"F4.wireOp",EDGE,"E16"),subQ1])],"isStart":true}),"instanceName":"1"})])],"derivedFrom":subQ3})]});}
            var Q8;
            {var subQ0=sQuery(id+"F4.wireOp",EDGE,"E7");var subQ1=sQuery(id+"F8.wireOp",EDGE,"E22");var subQ2=makeQuery(id+"F9.opSweep","SWEPT_FACE",FACE,{"disambiguationData":[OSD([subQ0,subQ1])]});Q8=makeQuery(id+"F15.opBoolean","INTERSECT",EDGE,{"disambiguationData":[OD(0.0)],"derivedFrom":[makeQuery(id+"F1.opRevolve","SWEPT_FACE",FACE,{"disambiguationData":[OSD([sQuery(id+"F0.wireOp",EDGE,"E1")])]}),makeQuery(id+"F14.opPattern","COPY",FACE,{"derivedFrom":makeQuery(id+"F11.opBoolean","SPLIT",FACE,{"disambiguationData":[TD([makeQuery(id+"F9.opSweep","CAP_FACE",FACE,{"disambiguationData":[OSD([subQ0,sQuery(id+"F4.wireOp",EDGE,"E16"),subQ1])],"isStart":true})])],"derivedFrom":subQ2}),"instanceName":"1"})]});}
            var Q9;
            {var subQ0=sQuery(id+"F4.wireOp",EDGE,"E7");var subQ1=sQuery(id+"F8.wireOp",EDGE,"E22");var subQ2=makeQuery(id+"F9.opSweep","SWEPT_FACE",FACE,{"disambiguationData":[OSD([subQ0,subQ1])]});var subQ3=makeQuery(id+"F10.opPattern","COPY",FACE,{"derivedFrom":subQ2,"instanceName":"1"});Q9=makeQuery(id+"F15.opBoolean","INTERSECT",EDGE,{"disambiguationData":[OD(0.0)],"derivedFrom":[makeQuery(id+"F1.opRevolve","SWEPT_FACE",FACE,{"disambiguationData":[OSD([sQuery(id+"F0.wireOp",EDGE,"E1")])]}),makeQuery(id+"F14.opPattern","COPY",FACE,{"derivedFrom":makeQuery(id+"F11.opBoolean","SPLIT",FACE,{"disambiguationData":[TD([makeQuery(id+"F10.opPattern","COPY",FACE,{"derivedFrom":makeQuery(id+"F9.opSweep","CAP_FACE",FACE,{"disambiguationData":[OSD([subQ0,sQuery(id+"F4.wireOp",EDGE,"E16"),subQ1])],"isStart":true}),"instanceName":"1"})])],"derivedFrom":subQ3}),"instanceName":"1"})]});}
            var Q10;
            {var subQ0=sQuery(id+"F4.wireOp",EDGE,"E7");var subQ1=sQuery(id+"F8.wireOp",EDGE,"E22");var subQ2=makeQuery(id+"F9.opSweep","SWEPT_FACE",FACE,{"disambiguationData":[OSD([subQ0,subQ1])]});Q10=makeQuery(id+"F15.opBoolean","INTERSECT",EDGE,{"disambiguationData":[OD(0.0)],"derivedFrom":[makeQuery(id+"F1.opRevolve","SWEPT_FACE",FACE,{"disambiguationData":[OSD([sQuery(id+"F0.wireOp",EDGE,"E1")])]}),makeQuery(id+"F14.opPattern","COPY",FACE,{"derivedFrom":makeQuery(id+"F11.opBoolean","SPLIT",FACE,{"disambiguationData":[TD([makeQuery(id+"F9.opSweep","CAP_FACE",FACE,{"disambiguationData":[OSD([subQ0,sQuery(id+"F4.wireOp",EDGE,"E16"),subQ1])],"isStart":true})])],"derivedFrom":subQ2}),"instanceName":"2"})]});}
            var Q11;
            {var subQ0=sQuery(id+"F4.wireOp",EDGE,"E7");var subQ1=sQuery(id+"F8.wireOp",EDGE,"E22");var subQ2=makeQuery(id+"F9.opSweep","SWEPT_FACE",FACE,{"disambiguationData":[OSD([subQ0,subQ1])]});var subQ3=makeQuery(id+"F10.opPattern","COPY",FACE,{"derivedFrom":subQ2,"instanceName":"1"});Q11=makeQuery(id+"F15.opBoolean","INTERSECT",EDGE,{"disambiguationData":[OD(0.0)],"derivedFrom":[makeQuery(id+"F1.opRevolve","SWEPT_FACE",FACE,{"disambiguationData":[OSD([sQuery(id+"F0.wireOp",EDGE,"E1")])]}),makeQuery(id+"F14.opPattern","COPY",FACE,{"derivedFrom":makeQuery(id+"F11.opBoolean","SPLIT",FACE,{"disambiguationData":[TD([makeQuery(id+"F10.opPattern","COPY",FACE,{"derivedFrom":makeQuery(id+"F9.opSweep","CAP_FACE",FACE,{"disambiguationData":[OSD([subQ0,sQuery(id+"F4.wireOp",EDGE,"E16"),subQ1])],"isStart":true}),"instanceName":"1"})])],"derivedFrom":subQ3}),"instanceName":"2"})]});}
            var Q12;
            {var subQ0=sQuery(id+"F4.wireOp",EDGE,"E7");var subQ1=sQuery(id+"F8.wireOp",EDGE,"E22");var subQ2=makeQuery(id+"F9.opSweep","SWEPT_FACE",FACE,{"disambiguationData":[OSD([subQ0,subQ1])]});var subQ3=makeQuery(id+"F10.opPattern","COPY",FACE,{"derivedFrom":subQ2,"instanceName":"1"});Q12=makeQuery(id+"F15.opBoolean","INTERSECT",EDGE,{"disambiguationData":[OD(0.0)],"derivedFrom":[makeQuery(id+"F1.opRevolve","SWEPT_FACE",FACE,{"disambiguationData":[OSD([sQuery(id+"F0.wireOp",EDGE,"E1")])]}),makeQuery(id+"F14.opPattern","COPY",FACE,{"derivedFrom":makeQuery(id+"F11.opBoolean","SPLIT",FACE,{"disambiguationData":[TD([makeQuery(id+"F10.opPattern","COPY",FACE,{"derivedFrom":makeQuery(id+"F9.opSweep","CAP_FACE",FACE,{"disambiguationData":[OSD([subQ0,sQuery(id+"F4.wireOp",EDGE,"E16"),subQ1])],"isStart":true}),"instanceName":"1"})])],"derivedFrom":subQ3}),"instanceName":"3"})]});}
            var Q13;
            {var subQ0=sQuery(id+"F4.wireOp",EDGE,"E7");var subQ1=sQuery(id+"F8.wireOp",EDGE,"E22");var subQ2=makeQuery(id+"F9.opSweep","SWEPT_FACE",FACE,{"disambiguationData":[OSD([subQ0,subQ1])]});Q13=makeQuery(id+"F15.opBoolean","INTERSECT",EDGE,{"disambiguationData":[OD(0.0)],"derivedFrom":[makeQuery(id+"F1.opRevolve","SWEPT_FACE",FACE,{"disambiguationData":[OSD([sQuery(id+"F0.wireOp",EDGE,"E1")])]}),makeQuery(id+"F14.opPattern","COPY",FACE,{"derivedFrom":makeQuery(id+"F11.opBoolean","SPLIT",FACE,{"disambiguationData":[TD([makeQuery(id+"F9.opSweep","CAP_FACE",FACE,{"disambiguationData":[OSD([subQ0,sQuery(id+"F4.wireOp",EDGE,"E16"),subQ1])],"isStart":true})])],"derivedFrom":subQ2}),"instanceName":"3"})]});}
            var Q14;
            {var subQ0=sQuery(id+"F4.wireOp",EDGE,"E7");var subQ1=sQuery(id+"F8.wireOp",EDGE,"E22");var subQ2=makeQuery(id+"F9.opSweep","SWEPT_FACE",FACE,{"disambiguationData":[OSD([subQ0,subQ1])]});Q14=makeQuery(id+"F15.opBoolean","INTERSECT",EDGE,{"disambiguationData":[OD(0.0)],"derivedFrom":[makeQuery(id+"F1.opRevolve","SWEPT_FACE",FACE,{"disambiguationData":[OSD([sQuery(id+"F0.wireOp",EDGE,"E1")])]}),makeQuery(id+"F14.opPattern","COPY",FACE,{"derivedFrom":makeQuery(id+"F11.opBoolean","SPLIT",FACE,{"disambiguationData":[TD([makeQuery(id+"F9.opSweep","CAP_FACE",FACE,{"disambiguationData":[OSD([subQ0,sQuery(id+"F4.wireOp",EDGE,"E16"),subQ1])],"isStart":true})])],"derivedFrom":subQ2}),"instanceName":"4"})]});}
            var Q15;
            {var subQ0=sQuery(id+"F4.wireOp",EDGE,"E7");var subQ1=sQuery(id+"F8.wireOp",EDGE,"E22");var subQ2=makeQuery(id+"F9.opSweep","SWEPT_FACE",FACE,{"disambiguationData":[OSD([subQ0,subQ1])]});var subQ3=makeQuery(id+"F10.opPattern","COPY",FACE,{"derivedFrom":subQ2,"instanceName":"1"});Q15=makeQuery(id+"F15.opBoolean","INTERSECT",EDGE,{"disambiguationData":[OD(0.0)],"derivedFrom":[makeQuery(id+"F1.opRevolve","SWEPT_FACE",FACE,{"disambiguationData":[OSD([sQuery(id+"F0.wireOp",EDGE,"E1")])]}),makeQuery(id+"F14.opPattern","COPY",FACE,{"derivedFrom":makeQuery(id+"F11.opBoolean","SPLIT",FACE,{"disambiguationData":[TD([makeQuery(id+"F10.opPattern","COPY",FACE,{"derivedFrom":makeQuery(id+"F9.opSweep","CAP_FACE",FACE,{"disambiguationData":[OSD([subQ0,sQuery(id+"F4.wireOp",EDGE,"E16"),subQ1])],"isStart":true}),"instanceName":"1"})])],"derivedFrom":subQ3}),"instanceName":"4"})]});}
            fillet(context, id + "F17", {"entities" : qUnion([Q0, Q1, Q2, Q3, Q4, Q5, Q6, Q7, Q8, Q9, Q10, Q11, Q12, Q13, Q14, Q15]), "radius" : 1 * mm, "tangentPropagation" : true, "allowEdgeOverflow" : false});
        }
        {
            var Q0;
            {var subQ0=sQuery(id+"F4.wireOp",EDGE,"E7");var subQ1=sQuery(id+"F8.wireOp",EDGE,"E22");var subQ2=makeQuery(id+"F9.opSweep","SWEPT_FACE",FACE,{"disambiguationData":[OSD([subQ0,subQ1])]});var subQ3=makeQuery(id+"F10.opPattern","COPY",FACE,{"derivedFrom":subQ2,"instanceName":"1"});var subQ4=makeQuery(id+"F9.opSweep","CAP_FACE",FACE,{"disambiguationData":[OSD([subQ0,sQuery(id+"F4.wireOp",EDGE,"E16"),subQ1])],"isStart":true});Q0=makeQuery(id+"F15.opBoolean","INTERSECT",EDGE,{"derivedFrom":[makeQuery(id+"F14.opPattern","COPY",FACE,{"derivedFrom":makeQuery(id+"F11.opBoolean","SPLIT",FACE,{"disambiguationData":[TD([makeQuery(id+"F10.opPattern","COPY",FACE,{"derivedFrom":subQ4,"instanceName":"1"})])],"derivedFrom":subQ3}),"instanceName":"5"}),makeQuery(id+"F14.opPattern","COPY",FACE,{"derivedFrom":makeQuery(id+"F11.opBoolean","SPLIT",FACE,{"disambiguationData":[TD([subQ4])],"derivedFrom":subQ2}),"instanceName":"6"})]});}
            var Q1;
            {var subQ0=sQuery(id+"F4.wireOp",EDGE,"E7");var subQ1=sQuery(id+"F8.wireOp",EDGE,"E22");var subQ2=makeQuery(id+"F9.opSweep","SWEPT_FACE",FACE,{"disambiguationData":[OSD([subQ0,subQ1])]});var subQ3=makeQuery(id+"F10.opPattern","COPY",FACE,{"derivedFrom":subQ2,"instanceName":"1"});var subQ4=makeQuery(id+"F9.opSweep","CAP_FACE",FACE,{"disambiguationData":[OSD([subQ0,sQuery(id+"F4.wireOp",EDGE,"E16"),subQ1])],"isStart":true});Q1=makeQuery(id+"F15.opBoolean","INTERSECT",EDGE,{"derivedFrom":[makeQuery(id+"F14.opPattern","COPY",FACE,{"derivedFrom":makeQuery(id+"F11.opBoolean","SPLIT",FACE,{"disambiguationData":[TD([makeQuery(id+"F10.opPattern","COPY",FACE,{"derivedFrom":subQ4,"instanceName":"1"})])],"derivedFrom":subQ3}),"instanceName":"6"}),makeQuery(id+"F14.opPattern","COPY",FACE,{"derivedFrom":makeQuery(id+"F11.opBoolean","SPLIT",FACE,{"disambiguationData":[TD([subQ4])],"derivedFrom":subQ2}),"instanceName":"7"})]});}
            var Q2;
            {var subQ0=sQuery(id+"F4.wireOp",EDGE,"E7");var subQ1=sQuery(id+"F8.wireOp",EDGE,"E22");var subQ2=makeQuery(id+"F9.opSweep","SWEPT_FACE",FACE,{"disambiguationData":[OSD([subQ0,subQ1])]});var subQ3=makeQuery(id+"F10.opPattern","COPY",FACE,{"derivedFrom":subQ2,"instanceName":"1"});var subQ4=makeQuery(id+"F9.opSweep","CAP_FACE",FACE,{"disambiguationData":[OSD([subQ0,sQuery(id+"F4.wireOp",EDGE,"E16"),subQ1])],"isStart":true});Q2=makeQuery(id+"F15.opBoolean","INTERSECT",EDGE,{"derivedFrom":[makeQuery(id+"F11.opBoolean","SPLIT",FACE,{"disambiguationData":[TD([subQ4])],"derivedFrom":subQ2}),makeQuery(id+"F14.opPattern","COPY",FACE,{"derivedFrom":makeQuery(id+"F11.opBoolean","SPLIT",FACE,{"disambiguationData":[TD([makeQuery(id+"F10.opPattern","COPY",FACE,{"derivedFrom":subQ4,"instanceName":"1"})])],"derivedFrom":subQ3}),"instanceName":"7"})]});}
            var Q3;
            {var subQ0=sQuery(id+"F4.wireOp",EDGE,"E7");var subQ1=sQuery(id+"F8.wireOp",EDGE,"E22");var subQ2=makeQuery(id+"F9.opSweep","SWEPT_FACE",FACE,{"disambiguationData":[OSD([subQ0,subQ1])]});var subQ3=makeQuery(id+"F10.opPattern","COPY",FACE,{"derivedFrom":subQ2,"instanceName":"1"});var subQ4=makeQuery(id+"F9.opSweep","CAP_FACE",FACE,{"disambiguationData":[OSD([subQ0,sQuery(id+"F4.wireOp",EDGE,"E16"),subQ1])],"isStart":true});Q3=makeQuery(id+"F15.opBoolean","INTERSECT",EDGE,{"derivedFrom":[makeQuery(id+"F11.opBoolean","SPLIT",FACE,{"disambiguationData":[TD([makeQuery(id+"F10.opPattern","COPY",FACE,{"derivedFrom":subQ4,"instanceName":"1"})])],"derivedFrom":subQ3}),makeQuery(id+"F14.opPattern","COPY",FACE,{"derivedFrom":makeQuery(id+"F11.opBoolean","SPLIT",FACE,{"disambiguationData":[TD([subQ4])],"derivedFrom":subQ2}),"instanceName":"1"})]});}
            var Q4;
            {var subQ0=sQuery(id+"F4.wireOp",EDGE,"E7");var subQ1=sQuery(id+"F8.wireOp",EDGE,"E22");var subQ2=makeQuery(id+"F9.opSweep","SWEPT_FACE",FACE,{"disambiguationData":[OSD([subQ0,subQ1])]});var subQ3=makeQuery(id+"F10.opPattern","COPY",FACE,{"derivedFrom":subQ2,"instanceName":"1"});var subQ4=makeQuery(id+"F9.opSweep","CAP_FACE",FACE,{"disambiguationData":[OSD([subQ0,sQuery(id+"F4.wireOp",EDGE,"E16"),subQ1])],"isStart":true});Q4=makeQuery(id+"F15.opBoolean","INTERSECT",EDGE,{"derivedFrom":[makeQuery(id+"F14.opPattern","COPY",FACE,{"derivedFrom":makeQuery(id+"F11.opBoolean","SPLIT",FACE,{"disambiguationData":[TD([makeQuery(id+"F10.opPattern","COPY",FACE,{"derivedFrom":subQ4,"instanceName":"1"})])],"derivedFrom":subQ3}),"instanceName":"1"}),makeQuery(id+"F14.opPattern","COPY",FACE,{"derivedFrom":makeQuery(id+"F11.opBoolean","SPLIT",FACE,{"disambiguationData":[TD([subQ4])],"derivedFrom":subQ2}),"instanceName":"2"})]});}
            var Q5;
            {var subQ0=sQuery(id+"F4.wireOp",EDGE,"E7");var subQ1=sQuery(id+"F8.wireOp",EDGE,"E22");var subQ2=makeQuery(id+"F9.opSweep","SWEPT_FACE",FACE,{"disambiguationData":[OSD([subQ0,subQ1])]});var subQ3=makeQuery(id+"F10.opPattern","COPY",FACE,{"derivedFrom":subQ2,"instanceName":"1"});var subQ4=makeQuery(id+"F9.opSweep","CAP_FACE",FACE,{"disambiguationData":[OSD([subQ0,sQuery(id+"F4.wireOp",EDGE,"E16"),subQ1])],"isStart":true});Q5=makeQuery(id+"F15.opBoolean","INTERSECT",EDGE,{"derivedFrom":[makeQuery(id+"F14.opPattern","COPY",FACE,{"derivedFrom":makeQuery(id+"F11.opBoolean","SPLIT",FACE,{"disambiguationData":[TD([makeQuery(id+"F10.opPattern","COPY",FACE,{"derivedFrom":subQ4,"instanceName":"1"})])],"derivedFrom":subQ3}),"instanceName":"2"}),makeQuery(id+"F14.opPattern","COPY",FACE,{"derivedFrom":makeQuery(id+"F11.opBoolean","SPLIT",FACE,{"disambiguationData":[TD([subQ4])],"derivedFrom":subQ2}),"instanceName":"3"})]});}
            var Q6;
            {var subQ0=sQuery(id+"F4.wireOp",EDGE,"E7");var subQ1=sQuery(id+"F8.wireOp",EDGE,"E22");var subQ2=makeQuery(id+"F9.opSweep","SWEPT_FACE",FACE,{"disambiguationData":[OSD([subQ0,subQ1])]});var subQ3=makeQuery(id+"F10.opPattern","COPY",FACE,{"derivedFrom":subQ2,"instanceName":"1"});var subQ4=makeQuery(id+"F9.opSweep","CAP_FACE",FACE,{"disambiguationData":[OSD([subQ0,sQuery(id+"F4.wireOp",EDGE,"E16"),subQ1])],"isStart":true});Q6=makeQuery(id+"F15.opBoolean","INTERSECT",EDGE,{"derivedFrom":[makeQuery(id+"F14.opPattern","COPY",FACE,{"derivedFrom":makeQuery(id+"F11.opBoolean","SPLIT",FACE,{"disambiguationData":[TD([makeQuery(id+"F10.opPattern","COPY",FACE,{"derivedFrom":subQ4,"instanceName":"1"})])],"derivedFrom":subQ3}),"instanceName":"3"}),makeQuery(id+"F14.opPattern","COPY",FACE,{"derivedFrom":makeQuery(id+"F11.opBoolean","SPLIT",FACE,{"disambiguationData":[TD([subQ4])],"derivedFrom":subQ2}),"instanceName":"4"})]});}
            var Q7;
            {var subQ0=sQuery(id+"F4.wireOp",EDGE,"E7");var subQ1=sQuery(id+"F8.wireOp",EDGE,"E22");var subQ2=makeQuery(id+"F9.opSweep","SWEPT_FACE",FACE,{"disambiguationData":[OSD([subQ0,subQ1])]});var subQ3=makeQuery(id+"F10.opPattern","COPY",FACE,{"derivedFrom":subQ2,"instanceName":"1"});var subQ4=makeQuery(id+"F9.opSweep","CAP_FACE",FACE,{"disambiguationData":[OSD([subQ0,sQuery(id+"F4.wireOp",EDGE,"E16"),subQ1])],"isStart":true});Q7=makeQuery(id+"F15.opBoolean","INTERSECT",EDGE,{"derivedFrom":[makeQuery(id+"F14.opPattern","COPY",FACE,{"derivedFrom":makeQuery(id+"F11.opBoolean","SPLIT",FACE,{"disambiguationData":[TD([makeQuery(id+"F10.opPattern","COPY",FACE,{"derivedFrom":subQ4,"instanceName":"1"})])],"derivedFrom":subQ3}),"instanceName":"4"}),makeQuery(id+"F14.opPattern","COPY",FACE,{"derivedFrom":makeQuery(id+"F11.opBoolean","SPLIT",FACE,{"disambiguationData":[TD([subQ4])],"derivedFrom":subQ2}),"instanceName":"5"})]});}
            fillet(context, id + "F18", {"entities" : qUnion([Q0, Q1, Q2, Q3, Q4, Q5, Q6, Q7]), "radius" : 1 * mm, "tangentPropagation" : true, "allowEdgeOverflow" : false});
        }
    });
